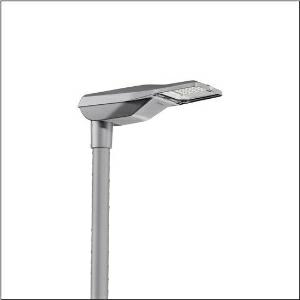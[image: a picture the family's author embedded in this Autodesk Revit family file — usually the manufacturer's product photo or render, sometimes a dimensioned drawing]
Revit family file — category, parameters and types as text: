
# Revit family: streetlight_sl_21_iq_micro___st1_0a_5xe1d31d08db_2abd
name_source: partatom
category: Lighting Fixtures
units: mm (PartAtom-declared; Revit-internal decimal feet)

## family parameters
Cut with Voids When Loaded = No
Host = Face
Light Source = No
Part Type = Normal
Room Calculation Point = No
Round Connector Dimension = Use Diameter
Shared = No

## types (1)
- --- (1 x LED, 4810 lm, 36.4 W, 3000K)
    Apparent Load = 36 VA
    CIE Flux Codes = 37 72 97 100 100
    Color Rendering = 70
    Color Temperature = 3000K
    Default Elevation = 1800 mm
    Description = Streetlight SL 21 iQ micro, mast luminaire, primary light control with lens, of PMMA, primary optical cover: cover, of toughened safety glass, transparent, light distribution: ST1.0a, light emission: direct distribution, primary light characteristic: asymmetric, installation type: post-top, side-entry, LED, High Power LED, rated luminous flux: 4.810lm, luminous efficacy: 132lm/W, light colour: 730, colour temperature: 3000K, control gear: iQ-Comfort, control: Auto-Match, Temp-Guard, Lumen-Switch, Night-Set, Smart-Wire, Light-Fading, Desk-Remote (wireless, voltage-free reading and setting of iQ features in the workshop via application-optimized NFC function/RFID function), optimised constant luminous flux control (CLO 2.0), pre-setting: linear dimming characteristic, mains connection: 220..240V, AC, 50/60Hz, start of lifetime: 36W, end of service life: 38W, reduction: 16W, luminaire housing, of diecast aluminium, powder-coated, SITECO metallic grey (DB 702S), corrosivity category C5 high according to DIN EN ISO 12944, please order mast flange separately, inclination adjustable: 0°, 5°, 10°, 15°, sealing non-destructively replaceable, multi-level sealing system, length: 528mm, width: 235mm, height: 110mm, mast flange for spigot size: 42mm (side-entry): 5XC10008XM4, 60/48mm (side-entry/post-top): 5XC10108XM2, 76/60mm (side-entry/post-top): 5XC10108XM1, protection rating (complete): IP66, insulation class (complete): insulation class II (safety insulation), certification: CE, ENEC, ENEC+, VDE, impact resistance: IK10, permissible operating ambient temperature for outdoor applications: -40..+50°C, standard-compliant lighting for roads and squares, packaging unit: 1 piece

Light Distribution: ST1.0a
    Height = 110 mm
    Lamp = 1 x LED
    Lamp Light Flux = 4810 lm
    Lamp Power = 36.4 W
    Lamp count = 1
    Length = 528 mm
    Luminous efficacy = 132 lm/W
    Manufacturer = Siteco
    ModVariant = No
    Model = 5XE1D31D08DB
    Number of Poles = 1
    OnlyDefault = Yes
    Power Factor = 1
    Product Name = Streetlight SL 21 iQ micro | ST1.0a
    Product group = mast luminaire | pylon top
    ProductGroupID = 6100
    Protection Class = Protection class II
    Protection Degree = IP 66
    RLX_Detail_Level = 1
    RLX_Emergency_Light_Flux = 0 lm
    RLX_Emergency_Type = 0
    RLX_Emergency_Type_DB = No
    RlxData = <blob elided: 99117 chars, md5=069d9292>
    Socket = socket
    Standby Power = 0 W
    System Light Flux = 4810 lm
    System Power = 36 W
    Type Comments = factory setting: luminous flux: 100 % | dim-lin: 254 | 715 mA
    Type Image = l_1006881.jpg
    URL = http://relux.com
    VarID = @adj_155517
    Voltage = 0 V
    Weight = 0.00 kg
    Width = 235 mm

## geometry (parser evidence)
native form markers: Blend x4, Sweep x10
no freeform markers — native parametric forms only
